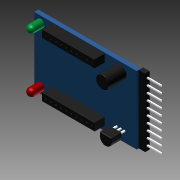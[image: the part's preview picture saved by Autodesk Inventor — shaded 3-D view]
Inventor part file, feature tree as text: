
AUTODESK INVENTOR PART (.ipt)
format: ipt  version: 2012 (Build 160160000, 160)  size: 502,784 bytes
history: native  units: in
note: dims shown in document units (in); Inventor stores cm internally (conversion verified against a paired STEP export)
features: extrude x9, fillet x4, sketch x3
ambient origin geometry x8: Origin, YZ Plane, XZ Plane, XY Plane, X Axis, Y Axis, Z Axis, Center Point
bodies: Solid1 (feature_tree)
feature tree (16):
  sketch  "Sketch1"  dims[d0=1.5748in d1=1.0433in]
  extrude  "Extrusion1"  Depth=1.0433in
  extrude  "Extrusion2"  Depth=0.1181in
  extrude  "Extrusion3"  Depth=0.1181in
  fillet  "Fillet1"  Radius=0.1181in
  fillet  "Fillet2"  Radius=0.0394in
  extrude  "Extrusion5"  Depth=0.0394in
  sketch  "Sketch3"  dims[d3=0.8071in d4=0.1181in]
  extrude  "Extrusion8"  Depth=0.1969in
  extrude  "Extrusion9"  Depth=0.1575in
  extrude  "Extrusion10"  Depth=0.0394in
  extrude  "Extrusion11"  Depth=0.063in TaperAngle=0.0deg
  fillet  "Fillet6"  Radius=0.2756in
  extrude  "Extrusion12"  Depth=0.1969in TaperAngle=0.0deg
  fillet  "Fillet7"  Radius=0.059in
  sketch  "Sketch4"  dims[d6=0.2756in d8=0.1181in d9=0.1181in d10=0.0394in d11=0.0394in d12=0.1969in d13=0.1575in d14=0.0394in d15=0.063in d16=0.0in d17=0.2756in d18=0.0in d19=0.1969in d20=0.0in d21=0.059in d22=0.01in d23=0.0591in d24=0.1772in d28=0.0394in d29=0.1575in d33=0.0197in d34=0.0197in d35=0.0197in d36=0.0197in d37=0.0197in d38=0.0197in d39=0.0394in d40=0.0394in d41=0.0197in d42=0.0197in d43=0.0197in d44=0.018in d45=0.0787in d46=0.0in d56=0.042in d58=0.042in d122=1.0433in d123=0.0669in d124=0.0197in d125=0.0197in d126=0.0615in d127=0.0236in d128=0.0197in d129=0.0197in d130=0.0197in d131=0.0197in d145=0.0236in d147=0.0236in d148=0.0197in d149=0.0197in d150=0.1in d151=0.0236in d152=0.1in d154=0.0197in d155=0.0197in d156=0.1in d157=0.0236in d158=0.0197in d159=0.0197in d160=0.1in d161=0.0236in d162=0.1in d163=0.0197in d164=0.0197in d166=0.1in d167=0.0236in d168=0.0197in d169=0.0197in d170=0.1in d171=0.0236in d172=0.0197in d173=0.0197in d174=0.1in d175=0.0236in d176=0.0197in d177=0.0197in d178=0.1in d179=0.0236in d180=0.315in d181=0.0in d182=0.0984in d183=0.0in d184=0.1181in d185=0.0in d191=0.0236in d192=0.0236in d193=0.043in d194=0.0472in d195=0.0236in d196=0.0236in d197=0.0787in d198=0.0472in d199=0.0236in d200=0.0236in d202=0.0472in d203=0.0236in d204=0.0236in d205=0.0787in d206=0.0787in d207=0.0787in d208=0.0236in d209=0.0236in d210=0.0472in d211=0.0236in d212=0.0236in d213=0.0787in d214=0.0472in d215=0.0236in d216=0.0236in d217=0.0787in d218=0.0472in d219=0.0236in d220=0.0236in d221=0.0787in d222=0.0472in d223=0.0236in d224=0.0236in d225=0.0787in d226=0.0472in d227=0.0236in d228=0.0236in d229=0.0787in d230=0.0472in d231=0.8071in d232=0.1181in d233=0.0236in d234=0.0236in d235=0.043in d236=0.0472in d237=0.0236in d238=0.0236in d239=0.0787in d240=0.0472in d241=0.0236in d242=0.0236in d243=0.0472in d244=0.0236in d245=0.0236in d246=0.0787in d247=0.0787in d248=0.0787in d249=0.0236in d250=0.0236in d251=0.0472in d252=0.0236in d253=0.0236in d254=0.0787in d255=0.0472in d256=0.0236in d257=0.0236in d258=0.0787in d259=0.0472in d260=0.0236in d261=0.0236in d262=0.0787in d263=0.0472in d264=0.0236in d265=0.0236in d266=0.0787in d267=0.0472in d268=0.0236in d269=0.0236in d270=0.0787in d271=0.0472in d274=0.7224in d275=0.2756in d276=0.1575in d277=0.0in d278=0.005in d279=0.1575in d280=0.0in d281=0.01in]
